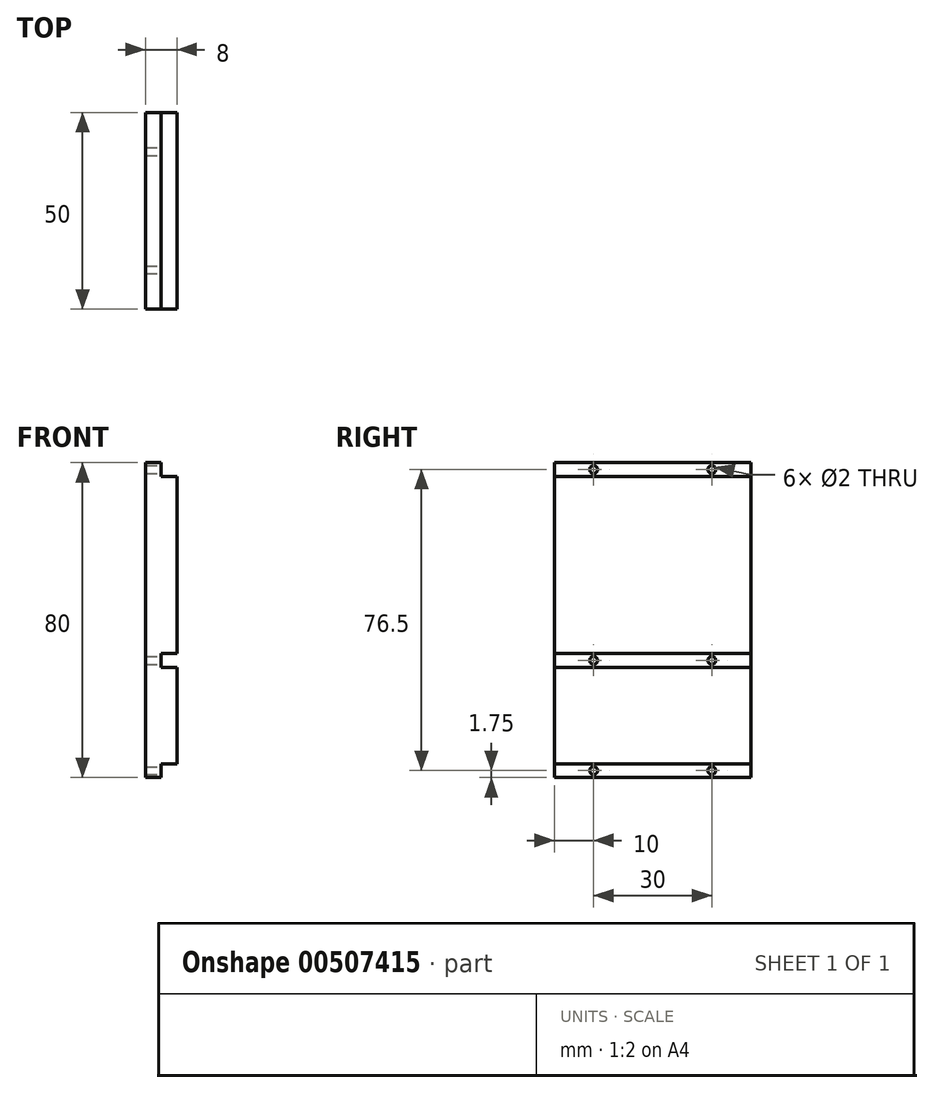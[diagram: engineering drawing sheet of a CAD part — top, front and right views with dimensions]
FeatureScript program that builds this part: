
annotation { "Feature Type Name" : "Feature", "Feature Type Description" : "" }
export const myFeature = defineFeature(function(context is Context, id is Id, definition is map)
    precondition{}
    {
        {
            var Q0;
            Q0=qCreatedBy(makeId("Right.planeOp"),FACE);
            var sketch = newSketch(context, id + "F0", { "sketchPlane" : qUnion([Q0])});
            skLineSegment(sketch, "E0.bottom", {"start": v(25, 40) * mm, "end": v(-25, 40) * mm});
            skLineSegment(sketch, "E0.top", {"start": v(25, -40) * mm, "end": v(-25, -40) * mm});
            skLineSegment(sketch, "E0.left", {"start": v(25, 40) * mm, "end": v(25, -40) * mm});
            skLineSegment(sketch, "E0.right", {"start": v(-25, 40) * mm, "end": v(-25, -40) * mm});
            skPoint(sketch, "E0.middle", {"position": v(0, 0) * mm});
            skSolve(sketch);
        }
        {
            var Q0;
            Q0=makeQuery(id+"F0.imprint","IMPRINT",FACE,{"disambiguationData":[TD([[makeQuery(id+"F0.imprint","IMPRINT",EDGE,{"derivedFrom":sQuery(id+"F0.wireOp",EDGE,"E0.bottom")}),1.0]])]});
            extrude(context, id + "F1", {"entities" : qUnion([Q0]), "endBound" : BoundingType.SYMMETRIC, "depth" : 8 * mm});
        }
        {
            var Q0;
            Q0=makeQuery(id+"F1.opExtrude","SWEPT_FACE",FACE,{"disambiguationData":[OSD([sQuery(id+"F0.wireOp",EDGE,"E0.right")])]});
            var sketch = newSketch(context, id + "F2", { "sketchPlane" : qUnion([Q0])});
            skPoint(sketch, "E1.firstSnap0", {"position": v(0, 40) * mm});
            skLineSegment(sketch, "E1.bottom", {"start": v(0, 40) * mm, "end": v(4, 40) * mm});
            skLineSegment(sketch, "E1.top", {"start": v(0, 36.5) * mm, "end": v(4, 36.5) * mm});
            skLineSegment(sketch, "E1.left", {"start": v(0, 40) * mm, "end": v(0, 36.5) * mm});
            skLineSegment(sketch, "E1.right", {"start": v(4, 40) * mm, "end": v(4, 36.5) * mm});
            skLineSegment(sketch, "E2.bottom", {"start": v(0, -8.5) * mm, "end": v(4, -8.5) * mm});
            skLineSegment(sketch, "E2.top", {"start": v(0, -12) * mm, "end": v(4, -12) * mm});
            skLineSegment(sketch, "E2.left", {"start": v(0, -8.5) * mm, "end": v(0, -12) * mm});
            skLineSegment(sketch, "E2.right", {"start": v(4, -8.5) * mm, "end": v(4, -12) * mm});
            skLineSegment(sketch, "E3.bottom", {"start": v(0, -36.5) * mm, "end": v(4, -36.5) * mm});
            skLineSegment(sketch, "E3.top", {"start": v(0, -40) * mm, "end": v(4, -40) * mm});
            skLineSegment(sketch, "E3.left", {"start": v(0, -36.5) * mm, "end": v(0, -40) * mm});
            skLineSegment(sketch, "E3.right", {"start": v(4, -36.5) * mm, "end": v(4, -40) * mm});
            skSolve(sketch);
        }
        {
            var Q0;
            Q0=makeQuery(id+"F2.imprint","IMPRINT",FACE,{"disambiguationData":[TD([[makeQuery(id+"F2.imprint","IMPRINT",EDGE,{"derivedFrom":sQuery(id+"F2.wireOp",EDGE,"E1.bottom")}),1.0]])]});
            var Q1;
            Q1=makeQuery(id+"F2.imprint","IMPRINT",FACE,{"disambiguationData":[TD([[makeQuery(id+"F2.imprint","IMPRINT",EDGE,{"derivedFrom":sQuery(id+"F2.wireOp",EDGE,"E2.bottom")}),-1.0]])]});
            var Q2;
            Q2=makeQuery(id+"F2.imprint","IMPRINT",FACE,{"disambiguationData":[TD([[makeQuery(id+"F2.imprint","IMPRINT",EDGE,{"derivedFrom":sQuery(id+"F2.wireOp",EDGE,"E3.bottom")}),-1.0]])]});
            extrude(context, id + "F3", {"entities" : qUnion([Q0, Q1, Q2]), "operationType" : NewBodyOperationType.REMOVE, "endBound" : BoundingType.THROUGH_ALL, "oppositeDirection" : true, "depth" : 25 * mm});
        }
        {
            var Q0;
            Q0=makeQuery(id+"F3.boolean.opBoolean","COPY",FACE,{"derivedFrom":makeQuery(id+"F3.opExtrude","SWEPT_FACE",FACE,{"disambiguationData":[OSD([sQuery(id+"F2.wireOp",EDGE,"E1.left")])]})});
            var sketch = newSketch(context, id + "F4", { "sketchPlane" : qUnion([Q0])});
            skCircle(sketch, "E4", {"center": v(-15, 38.25) * mm, "radius": 1 * mm});
            skCircle(sketch, "E5", {"center": v(15, 38.25) * mm, "radius": 1 * mm});
            skSolve(sketch);
        }
        {
            var Q0;
            Q0=makeQuery(id+"F4.imprint","IMPRINT",FACE,{"disambiguationData":[TD([[makeQuery(id+"F4.imprint","IMPRINT",EDGE,{"derivedFrom":sQuery(id+"F4.wireOp",EDGE,"E4")}),1.0]])]});
            var Q1;
            Q1=makeQuery(id+"F4.imprint","IMPRINT",FACE,{"disambiguationData":[TD([[makeQuery(id+"F4.imprint","IMPRINT",EDGE,{"derivedFrom":sQuery(id+"F4.wireOp",EDGE,"E5")}),1.0]])]});
            extrude(context, id + "F5", {"entities" : qUnion([Q0, Q1]), "operationType" : NewBodyOperationType.REMOVE, "endBound" : BoundingType.UP_TO_NEXT, "oppositeDirection" : true, "depth" : 25 * mm});
        }
        {
            var Q0;
            Q0=makeQuery(id+"F3.boolean.opBoolean","COPY",FACE,{"derivedFrom":makeQuery(id+"F3.opExtrude","SWEPT_FACE",FACE,{"disambiguationData":[OSD([sQuery(id+"F2.wireOp",EDGE,"E2.left")])]})});
            var sketch = newSketch(context, id + "F6", { "sketchPlane" : qUnion([Q0])});
            skCircle(sketch, "E6", {"center": v(-15, -10.25) * mm, "radius": 1 * mm});
            skCircle(sketch, "E7", {"center": v(15, -10.25) * mm, "radius": 1 * mm});
            skSolve(sketch);
        }
        {
            var Q0;
            Q0=makeQuery(id+"F6.imprint","IMPRINT",FACE,{"disambiguationData":[TD([[makeQuery(id+"F6.imprint","IMPRINT",EDGE,{"derivedFrom":sQuery(id+"F6.wireOp",EDGE,"E6")}),1.0]])]});
            var Q1;
            Q1=makeQuery(id+"F6.imprint","IMPRINT",FACE,{"disambiguationData":[TD([[makeQuery(id+"F6.imprint","IMPRINT",EDGE,{"derivedFrom":sQuery(id+"F6.wireOp",EDGE,"E7")}),1.0]])]});
            extrude(context, id + "F7", {"entities" : qUnion([Q0, Q1]), "operationType" : NewBodyOperationType.REMOVE, "endBound" : BoundingType.UP_TO_NEXT, "oppositeDirection" : true, "depth" : 25 * mm});
        }
        {
            var Q0;
            Q0=makeQuery(id+"F3.boolean.opBoolean","COPY",FACE,{"derivedFrom":makeQuery(id+"F3.opExtrude","SWEPT_FACE",FACE,{"disambiguationData":[OSD([sQuery(id+"F2.wireOp",EDGE,"E3.left")])]})});
            var sketch = newSketch(context, id + "F8", { "sketchPlane" : qUnion([Q0])});
            skCircle(sketch, "E8", {"center": v(-15, -38.25) * mm, "radius": 1 * mm});
            skCircle(sketch, "E9", {"center": v(15, -38.25) * mm, "radius": 1 * mm});
            skSolve(sketch);
        }
        {
            var Q0;
            Q0=makeQuery(id+"F8.imprint","IMPRINT",FACE,{"disambiguationData":[TD([[makeQuery(id+"F8.imprint","IMPRINT",EDGE,{"derivedFrom":sQuery(id+"F8.wireOp",EDGE,"E8")}),1.0]])]});
            var Q1;
            Q1=makeQuery(id+"F8.imprint","IMPRINT",FACE,{"disambiguationData":[TD([[makeQuery(id+"F8.imprint","IMPRINT",EDGE,{"derivedFrom":sQuery(id+"F8.wireOp",EDGE,"E9")}),1.0]])]});
            extrude(context, id + "F9", {"entities" : qUnion([Q0, Q1]), "operationType" : NewBodyOperationType.REMOVE, "endBound" : BoundingType.UP_TO_NEXT, "oppositeDirection" : true, "depth" : 25 * mm});
        }
    });
